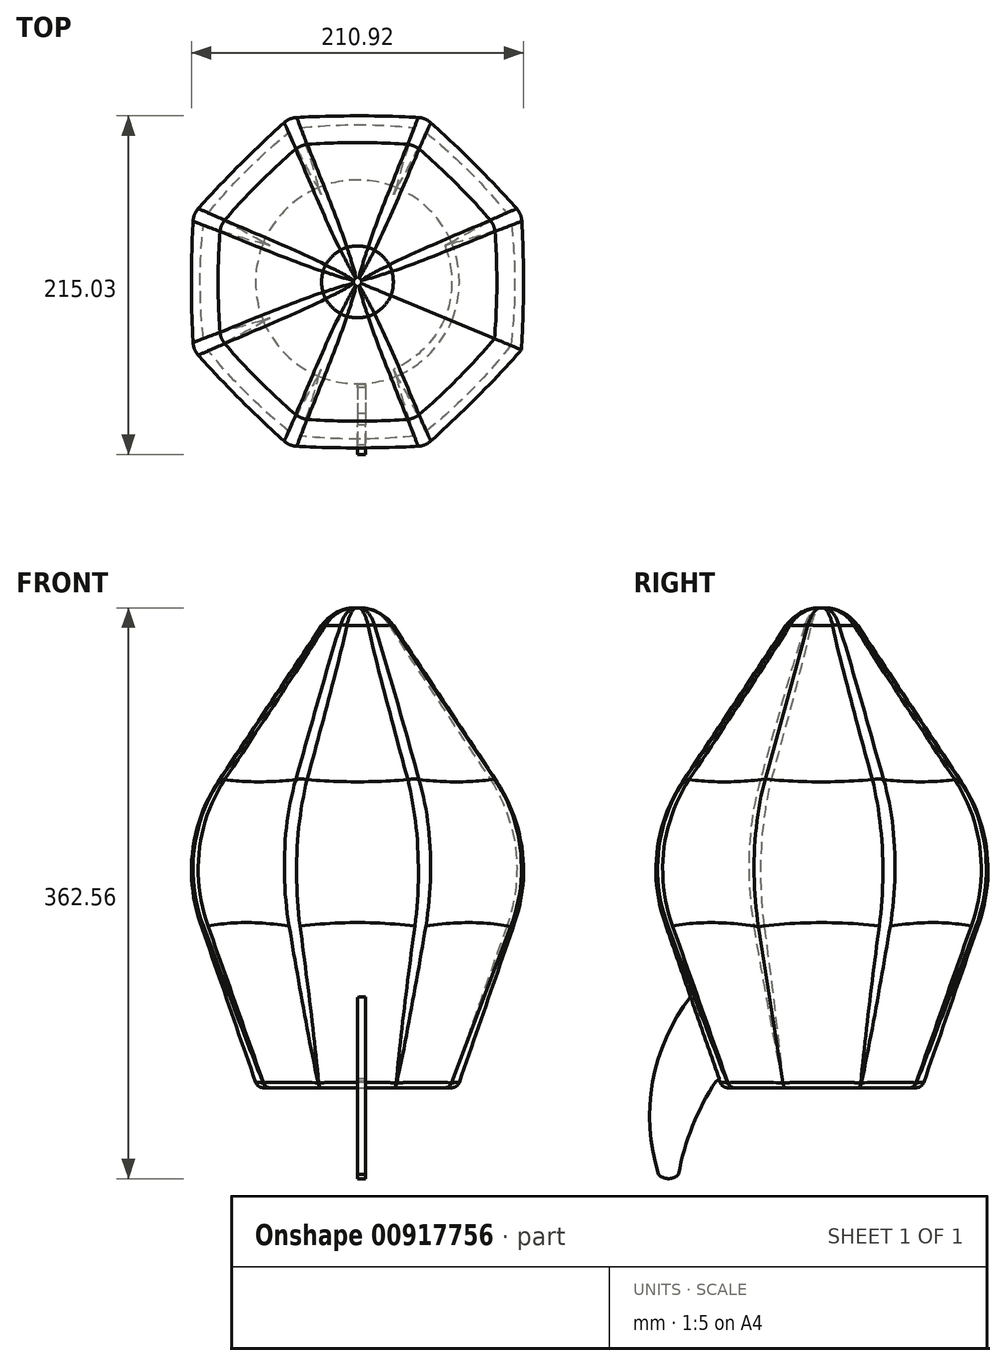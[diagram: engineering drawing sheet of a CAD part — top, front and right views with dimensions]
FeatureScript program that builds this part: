
annotation { "Feature Type Name" : "Feature", "Feature Type Description" : "" }
export const myFeature = defineFeature(function(context is Context, id is Id, definition is map)
    precondition{}
    {
        {
            var Q0;
            Q0=qCreatedBy(makeId("Top.planeOp"),FACE);
            var sketch = newSketch(context, id + "F0", { "sketchPlane" : qUnion([Q0])});
            skCircle(sketch, "E0.cCircle", {"center": v(0, 0) * mm, "radius": 116.32 * mm, "construction": true});
            skLineSegment(sketch, "E0.0", {"start": v(116.32, 48.18) * mm, "end": v(116.32, -48.18) * mm});
            skLineSegment(sketch, "E0.1", {"start": v(116.32, -48.18) * mm, "end": v(48.18, -116.32) * mm});
            skLineSegment(sketch, "E0.2", {"start": v(48.18, -116.32) * mm, "end": v(-48.18, -116.32) * mm});
            skLineSegment(sketch, "E0.3", {"start": v(-48.18, -116.32) * mm, "end": v(-116.32, -48.18) * mm});
            skLineSegment(sketch, "E0.4", {"start": v(-116.32, -48.18) * mm, "end": v(-116.32, 48.18) * mm});
            skLineSegment(sketch, "E0.5", {"start": v(-116.32, 48.18) * mm, "end": v(-48.18, 116.32) * mm});
            skLineSegment(sketch, "E0.6", {"start": v(-48.18, 116.32) * mm, "end": v(48.18, 116.32) * mm});
            skLineSegment(sketch, "E0.7", {"start": v(48.18, 116.32) * mm, "end": v(116.32, 48.18) * mm});
            skPoint(sketch, "E0.0.midPoint", {"position": v(116.32, 0) * mm});
            skSolve(sketch);
        }
        {
            var Q0;
            Q0=qCreatedBy(makeId("Top.planeOp"),FACE);
            cPlane(context, id + "F1", {"entities" : qUnion([Q0]), "cplaneType" : CPlaneType.OFFSET, "offset" : 152.4 * mm, "oppositeDirection" : true, "width" : 152.4 * mm, "height" : 152.4 * mm});
        }
        {
            var Q0;
            Q0=qCreatedBy(makeId("Top.planeOp"),FACE);
            cPlane(context, id + "F2", {"entities" : qUnion([Q0]), "cplaneType" : CPlaneType.OFFSET, "offset" : 152.4 * mm, "width" : 152.4 * mm, "height" : 152.4 * mm});
        }
        {
            var Q0;
            Q0=qCreatedBy(id+"F2.planeOp",FACE);
            var sketch = newSketch(context, id + "F3", { "sketchPlane" : qUnion([Q0])});
            skCircle(sketch, "E1", {"center": v(0, 0) * mm, "radius": 15.24 * mm});
            skSolve(sketch);
        }
        {
            var Q0;
            Q0=qCreatedBy(id+"F1.planeOp",FACE);
            var sketch = newSketch(context, id + "F4", { "sketchPlane" : qUnion([Q0])});
            skCircle(sketch, "E2", {"center": v(0, 0) * mm, "radius": 63.5 * mm});
            skSolve(sketch);
        }
        {
            var Q0;
            Q0=makeQuery(id+"F3.imprint","IMPRINT",FACE,{"disambiguationData":[TD([[makeQuery(id+"F3.imprint","IMPRINT",EDGE,{"derivedFrom":sQuery(id+"F3.wireOp",EDGE,"E1")}),1.0]])]});
            var Q1;
            Q1=makeQuery(id+"F0.imprint","IMPRINT",FACE,{"disambiguationData":[TD([[makeQuery(id+"F0.imprint","IMPRINT",EDGE,{"derivedFrom":sQuery(id+"F0.wireOp",EDGE,"E0.0")}),-1.0]])]});
            loft(context, id + "F5", {"sheetProfilesArray" : [{ "sheetProfileEntities" : qUnion([Q0]) }, { "sheetProfileEntities" : qUnion([Q1]) }]});
        }
        {
            var Q1;
            Q1=makeQuery(id+"F5.opLoft","CAP_FACE",FACE,{"disambiguationData":[OSD([makeQuery(id+"F0.imprint","IMPRINT",FACE,{"disambiguationData":[TD([[makeQuery(id+"F0.imprint","IMPRINT",EDGE,{"derivedFrom":sQuery(id+"F0.wireOp",EDGE,"E0.0")}),-1.0]])]})])],"isStart":true});
            var Q2;
            Q2=makeQuery(id+"F4.imprint","IMPRINT",FACE,{"disambiguationData":[TD([[makeQuery(id+"F4.imprint","IMPRINT",EDGE,{"derivedFrom":sQuery(id+"F4.wireOp",EDGE,"E2")}),1.0]])]});
            loft(context, id + "F6", {"operationType" : NewBodyOperationType.ADD, "sheetProfilesArray" : [{ "sheetProfileEntities" : qUnion([Q1]) }, { "sheetProfileEntities" : qUnion([Q2]) }]});
        }
        {
            var Q0;
            Q0=makeQuery(id+"F5.opLoft","MID_CAP_EDGE",EDGE,{"disambiguationData":[OSD([sQuery(id+"F0.wireOp",EDGE,"E0.0"),sQuery(id+"F0.wireOp",EDGE,"E0.7"),sQuery(id+"F3.wireOp",EDGE,"E1")])],"capPos":0.0});
            var Q1;
            Q1=makeQuery(id+"F5.opLoft","MID_CAP_EDGE",EDGE,{"disambiguationData":[OSD([sQuery(id+"F0.wireOp",EDGE,"E0.0"),sQuery(id+"F0.wireOp",EDGE,"E0.5"),sQuery(id+"F0.wireOp",EDGE,"E0.6"),sQuery(id+"F0.wireOp",EDGE,"E0.7"),sQuery(id+"F3.wireOp",EDGE,"E1")])],"capPos":0.0});
            var Q2;
            Q2=makeQuery(id+"F5.opLoft","MID_CAP_EDGE",EDGE,{"disambiguationData":[OSD([sQuery(id+"F0.wireOp",EDGE,"E0.4"),sQuery(id+"F0.wireOp",EDGE,"E0.5"),sQuery(id+"F0.wireOp",EDGE,"E0.6"),sQuery(id+"F3.wireOp",EDGE,"E1")])],"capPos":0.0});
            var Q3;
            Q3=makeQuery(id+"F5.opLoft","MID_CAP_EDGE",EDGE,{"disambiguationData":[OSD([sQuery(id+"F0.wireOp",EDGE,"E0.3"),sQuery(id+"F0.wireOp",EDGE,"E0.4"),sQuery(id+"F0.wireOp",EDGE,"E0.5"),sQuery(id+"F3.wireOp",EDGE,"E1")])],"capPos":0.0});
            var Q4;
            Q4=makeQuery(id+"F5.opLoft","MID_CAP_EDGE",EDGE,{"disambiguationData":[OSD([sQuery(id+"F0.wireOp",EDGE,"E0.0"),sQuery(id+"F0.wireOp",EDGE,"E0.1"),sQuery(id+"F0.wireOp",EDGE,"E0.7"),sQuery(id+"F3.wireOp",EDGE,"E1")])],"capPos":0.0});
            var Q5;
            Q5=makeQuery(id+"F5.opLoft","MID_CAP_EDGE",EDGE,{"disambiguationData":[OSD([sQuery(id+"F0.wireOp",EDGE,"E0.0"),sQuery(id+"F0.wireOp",EDGE,"E0.1"),sQuery(id+"F0.wireOp",EDGE,"E0.2"),sQuery(id+"F3.wireOp",EDGE,"E1")])],"capPos":0.0});
            var Q6;
            Q6=makeQuery(id+"F5.opLoft","MID_CAP_EDGE",EDGE,{"disambiguationData":[OSD([sQuery(id+"F0.wireOp",EDGE,"E0.2"),sQuery(id+"F0.wireOp",EDGE,"E0.3"),sQuery(id+"F0.wireOp",EDGE,"E0.4"),sQuery(id+"F3.wireOp",EDGE,"E1")])],"capPos":0.0});
            var Q7;
            Q7=makeQuery(id+"F5.opLoft","MID_CAP_EDGE",EDGE,{"disambiguationData":[OSD([sQuery(id+"F0.wireOp",EDGE,"E0.1"),sQuery(id+"F0.wireOp",EDGE,"E0.2"),sQuery(id+"F0.wireOp",EDGE,"E0.3"),sQuery(id+"F3.wireOp",EDGE,"E1")])],"capPos":0.0});
            fillet(context, id + "F7", {"entities" : qUnion([Q0, Q1, Q2, Q3, Q4, Q5, Q6, Q7]), "radius" : 25.4 * mm, "tangentPropagation" : true, "allowEdgeOverflow" : false});
        }
        {
            var Q0;
            {var subQ0=sQuery(id+"F0.wireOp",EDGE,"E0.3");var subQ1=sQuery(id+"F0.wireOp",EDGE,"E0.2");var subQ2=sQuery(id+"F0.wireOp",EDGE,"E0.1");Q0=makeQuery(id+"F6.boolean.opBoolean","MERGE",EDGE,{"derivedFrom":[makeQuery(id+"F5.opLoft","MID_CAP_EDGE",EDGE,{"disambiguationData":[OSD([subQ2,subQ1,subQ0])],"capPos":1.0}),makeQuery(id+"F6.opLoft","MID_CAP_EDGE",EDGE,{"disambiguationData":[OSD([subQ2,subQ1,subQ0])],"capPos":0.0})]});}
            var Q1;
            {var subQ0=sQuery(id+"F0.wireOp",EDGE,"E0.2");var subQ1=sQuery(id+"F0.wireOp",EDGE,"E0.1");var subQ2=sQuery(id+"F0.wireOp",EDGE,"E0.0");Q1=makeQuery(id+"F6.boolean.opBoolean","MERGE",EDGE,{"derivedFrom":[makeQuery(id+"F5.opLoft","MID_CAP_EDGE",EDGE,{"disambiguationData":[OSD([subQ2,subQ1,subQ0])],"capPos":1.0}),makeQuery(id+"F6.opLoft","MID_CAP_EDGE",EDGE,{"disambiguationData":[OSD([subQ2,subQ1,subQ0])],"capPos":0.0})]});}
            var Q2;
            {var subQ0=sQuery(id+"F0.wireOp",EDGE,"E0.7");var subQ1=sQuery(id+"F0.wireOp",EDGE,"E0.1");var subQ2=sQuery(id+"F0.wireOp",EDGE,"E0.0");Q2=makeQuery(id+"F6.boolean.opBoolean","MERGE",EDGE,{"derivedFrom":[makeQuery(id+"F5.opLoft","MID_CAP_EDGE",EDGE,{"disambiguationData":[OSD([subQ2,subQ1,subQ0])],"capPos":1.0}),makeQuery(id+"F6.opLoft","MID_CAP_EDGE",EDGE,{"disambiguationData":[OSD([subQ2,subQ1,subQ0])],"capPos":0.0})]});}
            var Q3;
            {var subQ0=sQuery(id+"F0.wireOp",EDGE,"E0.7");var subQ1=sQuery(id+"F0.wireOp",EDGE,"E0.6");var subQ2=sQuery(id+"F0.wireOp",EDGE,"E0.0");Q3=makeQuery(id+"F6.boolean.opBoolean","MERGE",EDGE,{"derivedFrom":[makeQuery(id+"F5.opLoft","MID_CAP_EDGE",EDGE,{"disambiguationData":[OSD([subQ2,subQ1,subQ0])],"capPos":1.0}),makeQuery(id+"F6.opLoft","MID_CAP_EDGE",EDGE,{"disambiguationData":[OSD([subQ2,subQ1,subQ0])],"capPos":0.0})]});}
            var Q4;
            {var subQ0=sQuery(id+"F0.wireOp",EDGE,"E0.7");var subQ1=sQuery(id+"F0.wireOp",EDGE,"E0.6");var subQ2=sQuery(id+"F0.wireOp",EDGE,"E0.5");Q4=makeQuery(id+"F6.boolean.opBoolean","MERGE",EDGE,{"derivedFrom":[makeQuery(id+"F5.opLoft","MID_CAP_EDGE",EDGE,{"disambiguationData":[OSD([subQ2,subQ1,subQ0])],"capPos":1.0}),makeQuery(id+"F6.opLoft","MID_CAP_EDGE",EDGE,{"disambiguationData":[OSD([subQ2,subQ1,subQ0])],"capPos":0.0})]});}
            var Q5;
            {var subQ0=sQuery(id+"F0.wireOp",EDGE,"E0.6");var subQ1=sQuery(id+"F0.wireOp",EDGE,"E0.5");var subQ2=sQuery(id+"F0.wireOp",EDGE,"E0.4");Q5=makeQuery(id+"F6.boolean.opBoolean","MERGE",EDGE,{"derivedFrom":[makeQuery(id+"F5.opLoft","MID_CAP_EDGE",EDGE,{"disambiguationData":[OSD([subQ2,subQ1,subQ0])],"capPos":1.0}),makeQuery(id+"F6.opLoft","MID_CAP_EDGE",EDGE,{"disambiguationData":[OSD([subQ2,subQ1,subQ0])],"capPos":0.0})]});}
            var Q6;
            {var subQ0=sQuery(id+"F0.wireOp",EDGE,"E0.5");var subQ1=sQuery(id+"F0.wireOp",EDGE,"E0.4");var subQ2=sQuery(id+"F0.wireOp",EDGE,"E0.3");Q6=makeQuery(id+"F6.boolean.opBoolean","MERGE",EDGE,{"derivedFrom":[makeQuery(id+"F5.opLoft","MID_CAP_EDGE",EDGE,{"disambiguationData":[OSD([subQ2,subQ1,subQ0])],"capPos":1.0}),makeQuery(id+"F6.opLoft","MID_CAP_EDGE",EDGE,{"disambiguationData":[OSD([subQ2,subQ1,subQ0])],"capPos":0.0})]});}
            var Q7;
            {var subQ0=sQuery(id+"F0.wireOp",EDGE,"E0.4");var subQ1=sQuery(id+"F0.wireOp",EDGE,"E0.3");var subQ2=sQuery(id+"F0.wireOp",EDGE,"E0.2");Q7=makeQuery(id+"F6.boolean.opBoolean","MERGE",EDGE,{"derivedFrom":[makeQuery(id+"F5.opLoft","MID_CAP_EDGE",EDGE,{"disambiguationData":[OSD([subQ2,subQ1,subQ0])],"capPos":1.0}),makeQuery(id+"F6.opLoft","MID_CAP_EDGE",EDGE,{"disambiguationData":[OSD([subQ2,subQ1,subQ0])],"capPos":0.0})]});}
            fillet(context, id + "F8", {"entities" : qUnion([Q0, Q1, Q2, Q3, Q4, Q5, Q6, Q7]), "radius" : 101.6 * mm, "tangentPropagation" : true, "allowEdgeOverflow" : false});
        }
        {
            var Q0;
            Q0=makeQuery(id+"F5.opLoft","SWEPT_EDGE",EDGE,{"disambiguationData":[OSD([sQuery(id+"F0.wireOp",EDGE,"E0.3"),sQuery(id+"F0.wireOp",EDGE,"E0.4"),sQuery(id+"F0.wireOp",EDGE,"E0.5"),sQuery(id+"F3.wireOp",EDGE,"E1")])]});
            var Q1;
            Q1=makeQuery(id+"F5.opLoft","SWEPT_EDGE",EDGE,{"disambiguationData":[OSD([sQuery(id+"F0.wireOp",EDGE,"E0.2"),sQuery(id+"F0.wireOp",EDGE,"E0.3"),sQuery(id+"F0.wireOp",EDGE,"E0.4"),sQuery(id+"F3.wireOp",EDGE,"E1")])]});
            var Q2;
            {var subQ0=sQuery(id+"F0.wireOp",EDGE,"E0.5");var subQ1=sQuery(id+"F0.wireOp",EDGE,"E0.4");var subQ2=sQuery(id+"F0.wireOp",EDGE,"E0.3");var subQ3=sQuery(id+"F0.wireOp",EDGE,"E0.2");Q2=makeQuery(id+"F8.opFillet","BLEND_EDGE",EDGE,{"blendedFrom":[makeQuery(id+"F6.boolean.opBoolean","MERGE",EDGE,{"derivedFrom":[makeQuery(id+"F5.opLoft","MID_CAP_EDGE",EDGE,{"disambiguationData":[OSD([subQ3,subQ2,subQ1])],"capPos":1.0}),makeQuery(id+"F6.opLoft","MID_CAP_EDGE",EDGE,{"disambiguationData":[OSD([subQ3,subQ2,subQ1])],"capPos":0.0})]}),makeQuery(id+"F6.boolean.opBoolean","MERGE",EDGE,{"derivedFrom":[makeQuery(id+"F5.opLoft","MID_CAP_EDGE",EDGE,{"disambiguationData":[OSD([subQ2,subQ1,subQ0])],"capPos":1.0}),makeQuery(id+"F6.opLoft","MID_CAP_EDGE",EDGE,{"disambiguationData":[OSD([subQ2,subQ1,subQ0])],"capPos":0.0})]})],"blendedInto":[]});}
            var Q3;
            Q3=makeQuery(id+"F5.opLoft","SWEPT_EDGE",EDGE,{"disambiguationData":[OSD([sQuery(id+"F0.wireOp",EDGE,"E0.1"),sQuery(id+"F0.wireOp",EDGE,"E0.2"),sQuery(id+"F0.wireOp",EDGE,"E0.3"),sQuery(id+"F3.wireOp",EDGE,"E1")])]});
            var Q4;
            Q4=makeQuery(id+"F5.opLoft","SWEPT_EDGE",EDGE,{"disambiguationData":[OSD([sQuery(id+"F0.wireOp",EDGE,"E0.0"),sQuery(id+"F0.wireOp",EDGE,"E0.1"),sQuery(id+"F0.wireOp",EDGE,"E0.2"),sQuery(id+"F3.wireOp",EDGE,"E1")])]});
            var Q5;
            Q5=makeQuery(id+"F5.opLoft","SWEPT_EDGE",EDGE,{"disambiguationData":[OSD([sQuery(id+"F0.wireOp",EDGE,"E0.0"),sQuery(id+"F0.wireOp",EDGE,"E0.1"),sQuery(id+"F0.wireOp",EDGE,"E0.7"),sQuery(id+"F3.wireOp",EDGE,"E1")])]});
            var Q6;
            Q6=makeQuery(id+"F5.opLoft","SWEPT_EDGE",EDGE,{"disambiguationData":[OSD([sQuery(id+"F0.wireOp",EDGE,"E0.0"),sQuery(id+"F0.wireOp",EDGE,"E0.7")])]});
            var Q7;
            Q7=makeQuery(id+"F5.opLoft","SWEPT_EDGE",EDGE,{"disambiguationData":[OSD([sQuery(id+"F0.wireOp",EDGE,"E0.5"),sQuery(id+"F0.wireOp",EDGE,"E0.6"),sQuery(id+"F0.wireOp",EDGE,"E0.7"),sQuery(id+"F3.wireOp",EDGE,"E1")])]});
            var Q8;
            Q8=makeQuery(id+"F5.opLoft","SWEPT_EDGE",EDGE,{"disambiguationData":[OSD([sQuery(id+"F0.wireOp",EDGE,"E0.4"),sQuery(id+"F0.wireOp",EDGE,"E0.5"),sQuery(id+"F0.wireOp",EDGE,"E0.6"),sQuery(id+"F3.wireOp",EDGE,"E1")])]});
            fillet(context, id + "F9", {"entities" : qUnion([Q0, Q1, Q2, Q3, Q4, Q5, Q6, Q7, Q8]), "radius" : 12.7 * mm, "tangentPropagation" : true, "allowEdgeOverflow" : false});
        }
        {
            var Q0;
            Q0=qCreatedBy(makeId("Right.planeOp"),FACE);
            var sketch = newSketch(context, id + "F10", { "sketchPlane" : qUnion([Q0])});
            skArc(sketch, "E3", {"start": v(-81.6, -92.6) * mm, "mid": v(-107.35, -147.22) * mm, "end": v(-103.8, -207.5) * mm});
            skArc(sketch, "E4", {"start": v(-103.8, -207.5) * mm, "mid": v(-97.43, -210.16) * mm, "end": v(-91.05, -207.5) * mm});
            skArc(sketch, "E5", {"start": v(-67.2, -148.33) * mm, "mid": v(-82.22, -176.67) * mm, "end": v(-91.05, -207.5) * mm});
            skArc(sketch, "E6", {"start": v(-67.2, -148.33) * mm, "mid": v(-55.34, -115.54) * mm, "end": v(-81.6, -92.6) * mm});
            skSolve(sketch);
        }
        {
            var Q0;
            Q0=makeQuery(id+"F10.imprint","IMPRINT",FACE,{"disambiguationData":[TD([[makeQuery(id+"F10.imprint","IMPRINT",EDGE,{"derivedFrom":sQuery(id+"F10.wireOp",EDGE,"E3")}),1.0]])]});
            extrude(context, id + "F11", {"entities" : qUnion([Q0]), "operationType" : NewBodyOperationType.ADD, "depth" : 5.08 * mm, "offsetDistance" : 25.4 * mm});
        }
        {
            var Q0;
            Q0=makeQuery(id+"F6.opLoft","CAP_FACE",FACE,{"disambiguationData":[OSD([makeQuery(id+"F4.imprint","IMPRINT",FACE,{"disambiguationData":[TD([[makeQuery(id+"F4.imprint","IMPRINT",EDGE,{"derivedFrom":sQuery(id+"F4.wireOp",EDGE,"E2")}),1.0]])]})])],"isStart":true});
            fillet(context, id + "F12", {"entities" : qUnion([Q0]), "radius" : 5.08 * mm, "tangentPropagation" : true, "allowEdgeOverflow" : false});
        }
        {
            var Q0;
            Q0=qCreatedBy(makeId("Top.planeOp"),FACE);
            cPlane(context, id + "F13", {"entities" : qUnion([Q0]), "cplaneType" : CPlaneType.OFFSET, "offset" : 57.15 * mm, "width" : 152.4 * mm, "height" : 152.4 * mm});
        }
    });
